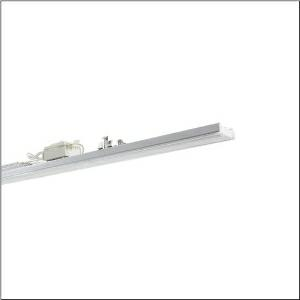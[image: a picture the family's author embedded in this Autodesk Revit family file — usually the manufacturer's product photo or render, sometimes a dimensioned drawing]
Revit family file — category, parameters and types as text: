
# Revit family: licross_21_recessed_mo_52tl19dn495g
name_source: partatom
category: Lighting Fixtures
units: mm (PartAtom-declared; Revit-internal decimal feet)

## family parameters
Cut with Voids When Loaded = No
Host = Face
Light Source = No
Part Type = Normal
Room Calculation Point = No
Round Connector Dimension = Use Diameter
Shared = No

## types (1)
- --- (1 x LED, 9850 lm, 58 W, 4000K)
    Apparent Load = 58 VA
    CIE Flux Codes = 55 90 98 100 100
    Color Rendering = 80
    Color Temperature = 4000K
    Default Elevation = 1800 mm
    Description = Licross 21 Recessed MO, luminaire insert, of sheet steel, galvanised, coil coated, white, length: 1.500mm, width: 66mm, height: 67mm, LED rated luminous flux: 9.850lm, light colour: 840, SDCM (Standard Deviation of Colour Matching)MacAdam ≤ 3 SDCM (initial), control gear: DALI 2, with plug, 5-pole, with phase selection, mains connection: 220..240V, AC, 50/60Hz, rated input power: 58W, internal wiring halogen-free, primary light control with lens, of plastic, primary optical cover: cover, of PMMA, light emission: direct distribution, primary light characteristic: double asymmetric, protection rating (complete): IP40, insulation class (complete): insulation class I (protective earthing), certification: CE, ENEC, VDE, UKCA, protection symbol: D if used in an environment without relevant dust loads with corresponding accessories, impact resistance: IK06, permissible ambient temperature for indoor applications: -25..+35°C, corresponds to IFS (International Featured Standards) requirements for safety and quality in the food industry, reducing of maximum allowable ambient temperature of 5°C with ceiling mounting, LABS conformity tested according to VDMA 24364:2018-05, The light source and the operating device comply with the requirements of the Ecodesign Regulation (EU) 2019/2020 and are replaceable in accordance with this regulation, packaging unit: 1 piece
    Height = 58 mm
    Lamp = 1 x LED
    Lamp Light Flux = 9850 lm
    Lamp Power = 58 W
    Lamp count = 1
    Length = 1500 mm
    Luminous efficacy = 170 lm/W
    Manufacturer = Siteco
    ModVariant = No
    Model = 52TL19DN495G
    Mounting Place = Ceiling
    Mounting Type = Pendant
    Number of Poles = 1
    OnlyDefault = Yes
    Power Factor = 1
    Product Name = Licross 21 Recessed MO
    Product group = luminaire insert | ceiling pendant
    ProductGroupID = 901
    Protection Class = Protection class I
    Protection Degree = IP 40
    RLX_Detail_Level = 1
    RLX_Emergency_Light_Flux = 0 lm
    RLX_Emergency_Type = 0
    RLX_Emergency_Type_DB = No
    RlxData = <blob elided: 24813 chars, md5=0e135059>
    Socket = socket
    Standby Power = 0 W
    System Light Flux = 9850 lm
    System Power = 58 W
    Type Comments = factory setting: luminous flux: 100 % | dim-lin: 254 | 390 mA
    Type Image = l_1296930.jpg
    URL = http://relux.com
    VarID = @adj_128133
    Voltage = 0 V
    Weight = 0.00 kg
    Width = 66 mm

## geometry (parser evidence)
native form markers: Blend x4, Sweep x14
no freeform markers — native parametric forms only
